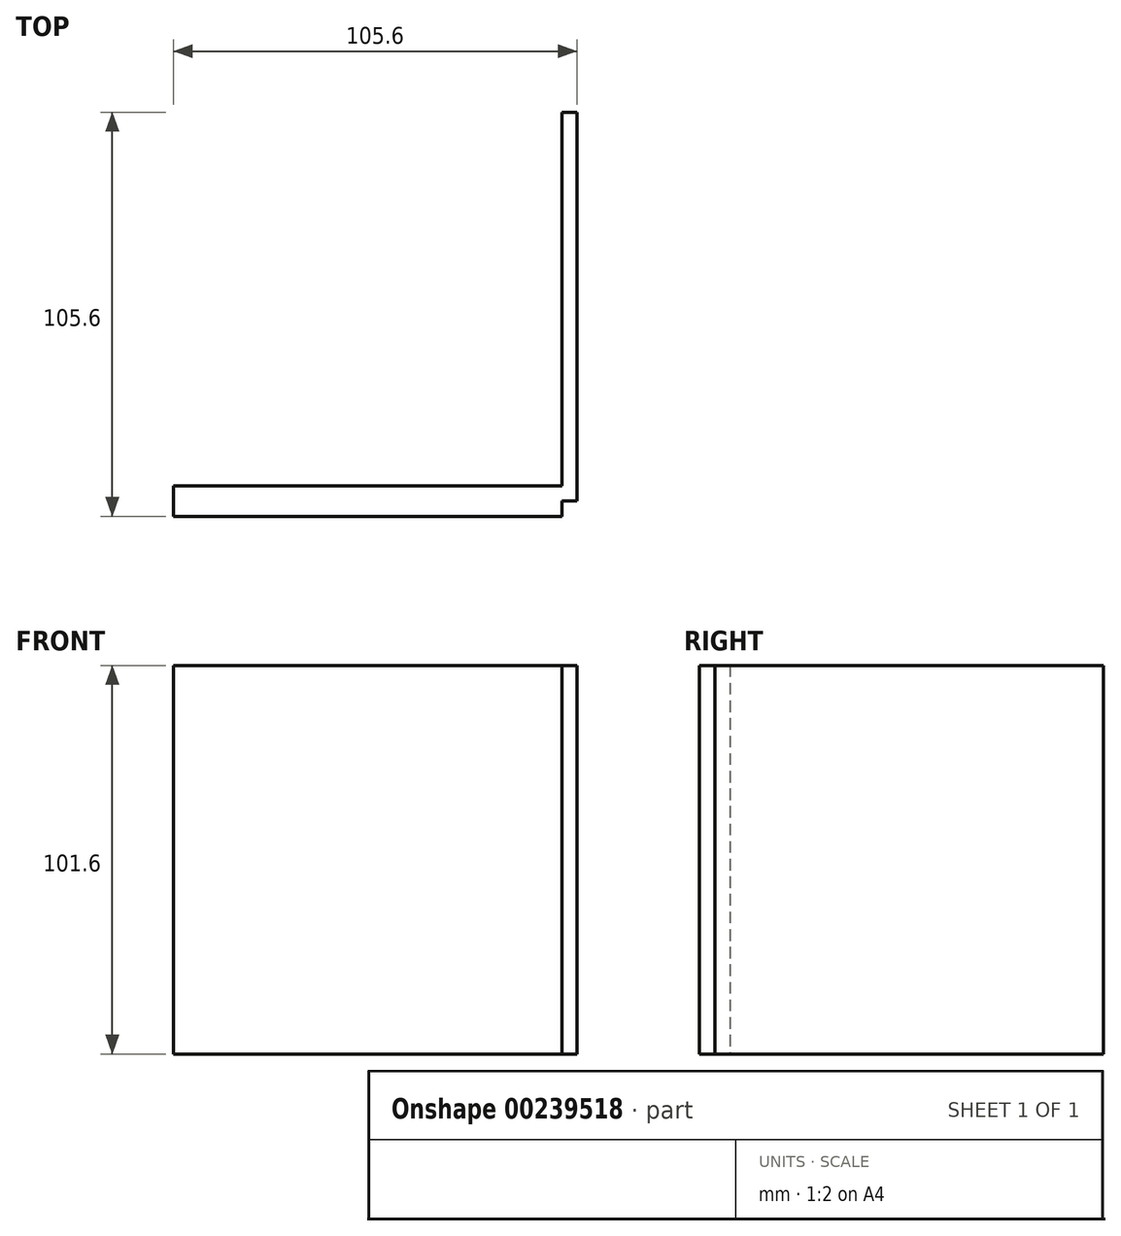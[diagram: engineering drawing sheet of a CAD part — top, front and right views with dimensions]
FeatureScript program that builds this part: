
annotation { "Feature Type Name" : "Feature", "Feature Type Description" : "" }
export const myFeature = defineFeature(function(context is Context, id is Id, definition is map)
    precondition{}
    {
        {
            assignVariable(context, id + "F0", {"name" : "P", "anyValue" : 4});
        }
        {
            var Q0;
            Q0=qCreatedBy(makeId("Front.planeOp"),FACE);
            var sketch = newSketch(context, id + "F1", { "sketchPlane" : qUnion([Q0])});
            skLineSegment(sketch, "E0.bottom", {"start": v(-50.8, 50.8) * mm, "end": v(50.8, 50.8) * mm});
            skLineSegment(sketch, "E0.top", {"start": v(-50.8, -50.8) * mm, "end": v(50.8, -50.8) * mm});
            skLineSegment(sketch, "E0.left", {"start": v(-50.8, 50.8) * mm, "end": v(-50.8, -50.8) * mm});
            skLineSegment(sketch, "E0.right", {"start": v(50.8, 50.8) * mm, "end": v(50.8, -50.8) * mm});
            skPoint(sketch, "E0.middle", {"position": v(0, 0) * mm});
            skSolve(sketch);
        }
        {
            var Q0;
            Q0 = qSketchRegion(id + "F1", true);
            extrude(context, id + "F2", {"entities" : qUnion([Q0]), "endBound" : BoundingType.SYMMETRIC, "depth" : ((2) * (getVariable(context, 'P'))) * mm});
        }
        {
            var Q0;
            Q0=makeQuery(id+"F2.opExtrude","SWEPT_FACE",FACE,{"disambiguationData":[OSD([sQuery(id+"F1.wireOp",EDGE,"E0.right")])]});
            var sketch = newSketch(context, id + "F3", { "sketchPlane" : qUnion([Q0])});
            skLineSegment(sketch, "E1.bottom", {"start": v(101.6, -50.8) * mm, "end": v(0, -50.8) * mm});
            skLineSegment(sketch, "E1.top", {"start": v(101.6, 50.8) * mm, "end": v(0, 50.8) * mm});
            skLineSegment(sketch, "E1.left", {"start": v(101.6, -50.8) * mm, "end": v(101.6, 50.8) * mm});
            skLineSegment(sketch, "E1.right", {"start": v(0, -50.8) * mm, "end": v(0, 50.8) * mm});
            skSolve(sketch);
        }
        {
            var Q0;
            Q0 = qSketchRegion(id + "F3", true);
            extrude(context, id + "F4", {"entities" : qUnion([Q0]), "operationType" : NewBodyOperationType.ADD, "depth" : (getVariable(context, 'P')) * mm});
        }
    });
